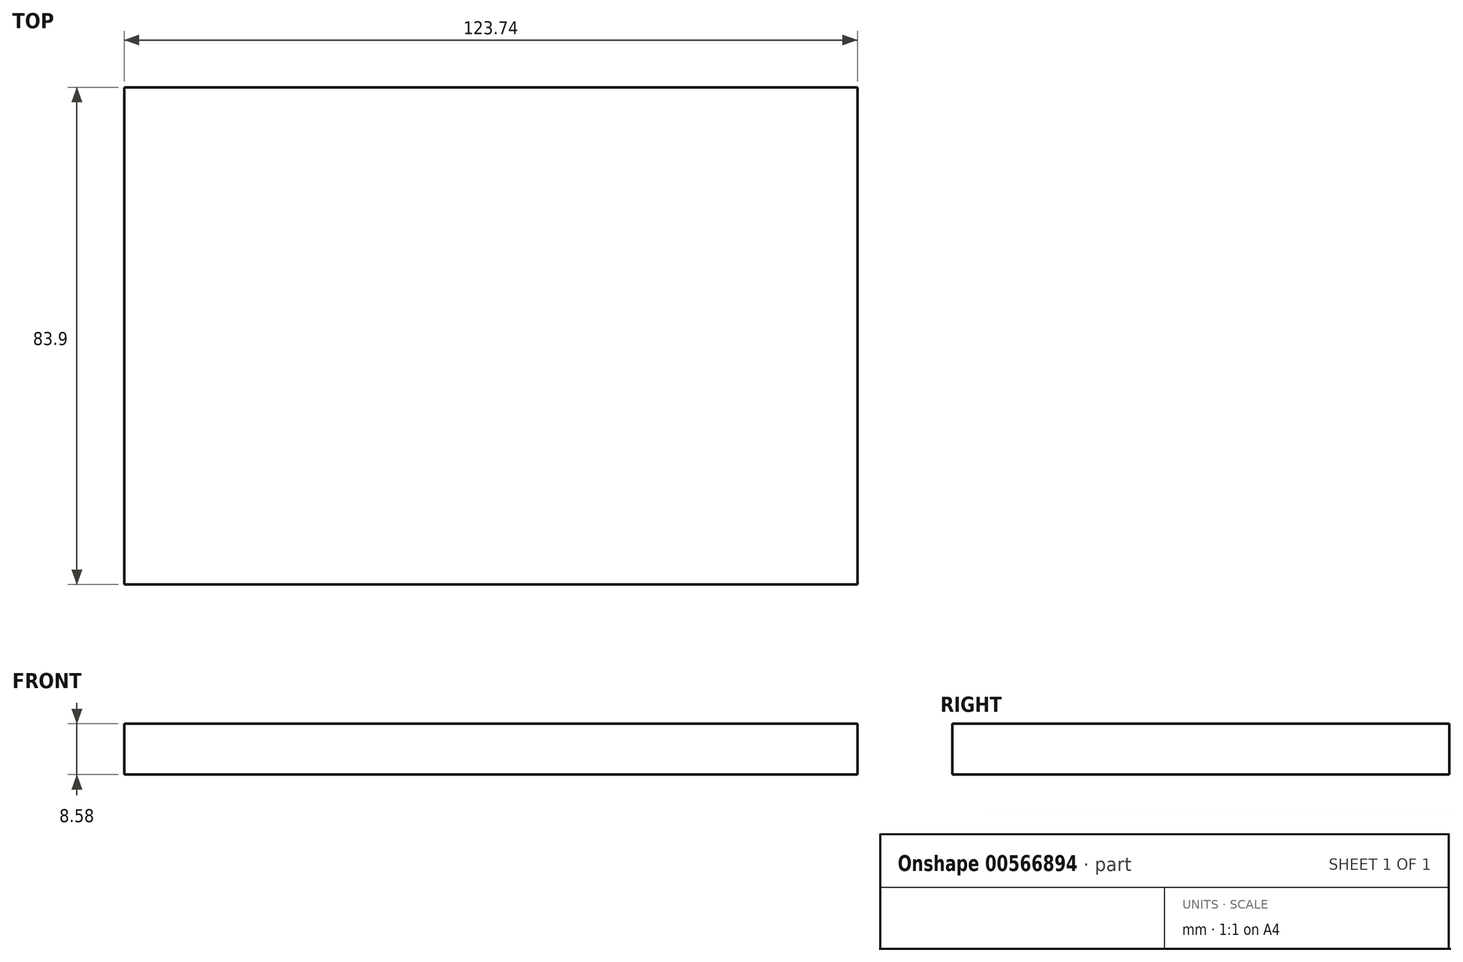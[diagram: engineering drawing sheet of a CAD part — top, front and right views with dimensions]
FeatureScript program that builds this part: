
annotation { "Feature Type Name" : "Feature", "Feature Type Description" : "" }
export const myFeature = defineFeature(function(context is Context, id is Id, definition is map)
    precondition{}
    {
        {
            var Q0;
            Q0=qCreatedBy(makeId("Front.planeOp"),FACE);
            var sketch = newSketch(context, id + "F0", { "sketchPlane" : qUnion([Q0])});
            skSolve(sketch);
        }
        {
            var Q0;
            Q0=qCreatedBy(makeId("Front.planeOp"),FACE);
            var sketch = newSketch(context, id + "F1", { "sketchPlane" : qUnion([Q0])});
            skLineSegment(sketch, "E0.bottom", {"start": v(-62.9, -66.16) * mm, "end": v(60.85, -66.16) * mm});
            skLineSegment(sketch, "E0.top", {"start": v(-62.9, -57.58) * mm, "end": v(60.85, -57.58) * mm});
            skLineSegment(sketch, "E0.left", {"start": v(-62.9, -66.16) * mm, "end": v(-62.9, -57.58) * mm});
            skLineSegment(sketch, "E0.right", {"start": v(60.85, -66.16) * mm, "end": v(60.85, -57.58) * mm});
            skSolve(sketch);
        }
        {
            var Q0;
            Q0 = qSketchRegion(id + "F1", true);
            extrude(context, id + "F2", {"entities" : qUnion([Q0]), "depth" : 83.9 * mm, "offsetDistance" : 25 * mm});
        }
    });
